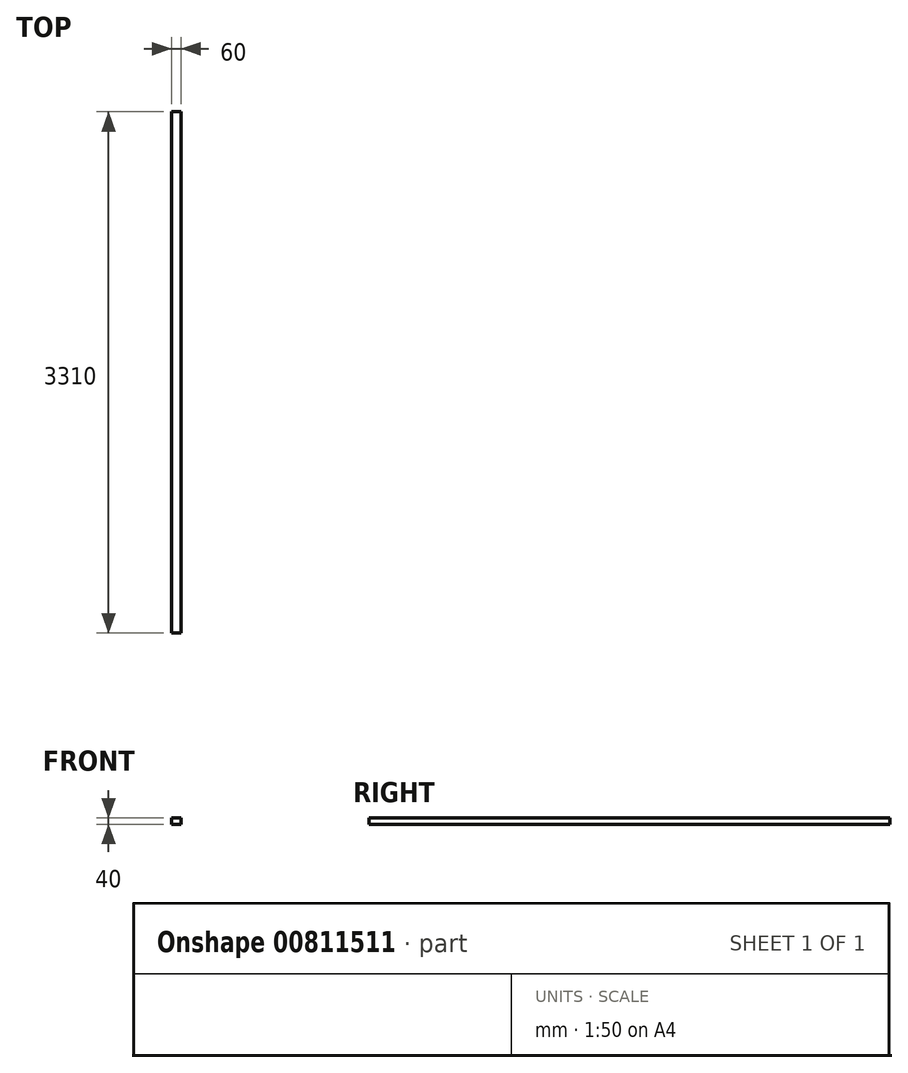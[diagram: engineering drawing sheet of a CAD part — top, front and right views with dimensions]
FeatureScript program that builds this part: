
annotation { "Feature Type Name" : "Feature", "Feature Type Description" : "" }
export const myFeature = defineFeature(function(context is Context, id is Id, definition is map)
    precondition{}
    {
        {
            var Q0;
            Q0=qCreatedBy(makeId("Top.planeOp"),FACE);
            var sketch = newSketch(context, id + "F0", { "sketchPlane" : qUnion([Q0])});
            skLineSegment(sketch, "E0.bottom", {"start": v(30, 1655) * mm, "end": v(-30, 1655) * mm});
            skLineSegment(sketch, "E0.top", {"start": v(30, -1655) * mm, "end": v(-30, -1655) * mm});
            skLineSegment(sketch, "E0.left", {"start": v(30, 1655) * mm, "end": v(30, -1655) * mm});
            skLineSegment(sketch, "E0.right", {"start": v(-30, 1655) * mm, "end": v(-30, -1655) * mm});
            skPoint(sketch, "E0.middle", {"position": v(0, 0) * mm});
            skSolve(sketch);
        }
        {
            var Q0;
            Q0=makeQuery(id+"F0.imprint","IMPRINT",FACE,{"disambiguationData":[TD([[makeQuery(id+"F0.imprint","IMPRINT",EDGE,{"derivedFrom":sQuery(id+"F0.wireOp",EDGE,"E0.bottom")}),1.0]])]});
            extrude(context, id + "F1", {"entities" : qUnion([Q0]), "depth" : 40 * mm, "offsetDistance" : 25 * mm});
        }
    });
